# Revit family: Heat Pump-Rheem-A2W-35kW-Horizontal
name_source: partatom
category: Mechanical Equipment
units: mm (PartAtom-declared; Revit-internal decimal feet)

## family parameters
Always vertical = Yes
Cut with Voids When Loaded = No
OmniClass Number = 23.75.10.21
OmniClass Title = Heat Pumps
Part Type = Normal
Room Calculation Point = No
Round Connector Dimension = Use Radius
Shared = No
Work Plane-Based = No

## types (4) — shared parameters
ApparentLoad_ANZRS = 35 kW
BodyWidth = 807 mm  [stored 2.64764 ft]
Height_ANZRS = 940 mm
InletPipeDiameter = 50 mm  [stored 0.164042 ft]
Length_ANZRS = 1805 mm  [stored 5.92192 ft]
Manufacturer = Rheem
Material_ANZRS = Rheem-Steel-Grey
OutletPipeDiameter = 50 mm  [stored 0.164042 ft]
PipeInsetSide = 147 mm
PowerFactor_ANZRS = 1
SupportInsetSide = 66 mm
URL = https://www.rheem.com.au
Voltage_ANZRS = 230 V
Wattage_ANZRS = 35 kW
calcFanGuardDepth = 133 mm  [stored 0.436352 ft]
calcInletPipeRadius = 25 mm  [stored 0.082021 ft]
calcOutletPipeRad = 25 mm  [stored 0.082021 ft]
zero-valued in all types: Default Elevation

## per-type parameters (varying)
| type | Description | Model | Show Fan Frame | Show Top Supports | Width_ANZRS | calcTopSupport |
| 953035H0 | Rheem's Commercial Air to Water (A2W) Heat Pump is designed with the commercial user in mind. A truly commercial grade heat pump that delivers hot water at 65°C with a system Coefficient of Performance (COP) up to 4.0. Non ducted models are generally designed for outdoor installations. Non ducted models may be installed indoors, without ducting, if a sufficient supply of heat energy is available. | Rheem Commercial Air to Water Heat Pump – 35kW Horizontal Discharge & Non Ducted | No | No | 588 mm | 0 mm  [stored 0 ft] |
| 953035HS | Rheem's Commercial Air to Water (A2W) Heat Pump is designed with the commercial user in mind. A truly commercial grade heat pump that delivers hot water at 65°C with a system Coefficient of Performance (COP) up to 4.0. Non ducted models are generally designed for outdoor installations. Non ducted models may be installed indoors, without ducting, if a sufficient supply of heat energy is available. Stackable models allow horizontal discharge units to be stacked two high for reduced footprint. | Rheem Commercial Air to Water Heat Pump – 35kW Non Ducted & Stacked | No | Yes | 588 mm | 37 mm  [stored 0.121391 ft] |
| 952035H0 | Rheem's Commercial Air to Water (A2W) Heat Pump is designed with the commercial user in mind. A truly commercial grade heat pump that delivers hot water at 65°C with a system Coefficient of Performance (COP) up to 4.0. Ducted models are designed to be connected to ducting to convey cold discharge air away from the heat pump air inlet if a sufficient supply of heat energy is not available in the installation area. | Rheem Commercial Air to Water Heat Pump – 35kW Horizontal Discharge & Ducted | Yes | No | 681 mm | 0 mm  [stored 0 ft] |
| 952035HS | Rheem's Commercial Air to Water (A2W) Heat Pump is designed with the commercial user in mind. A truly commercial grade heat pump that delivers hot water at 65°C with a system Coefficient of Performance (COP) up to 4.0. Ducted models are designed to be connected to ducting to convey cold discharge air away from the heat pump air inlet if a sufficient supply of heat energy is not available in the installation area. Stackable models allow horizontal discharge units to be stacked two high for reduced footprint. | Rheem Commercial Air to Water Heat Pump – 35kW Ducted & Stacked | Yes | Yes | 681 mm | 37 mm  [stored 0.121391 ft] |

note: column(s) folded — value = type name in every type: ProductCode_ANZRS

note: [stored X ft] marks values corroborated as IEEE doubles in the binary element streams (Revit-internal decimal feet)

## geometry (parser evidence)
native form markers: Blend x4, Sweep x9
no freeform markers — native parametric forms only
